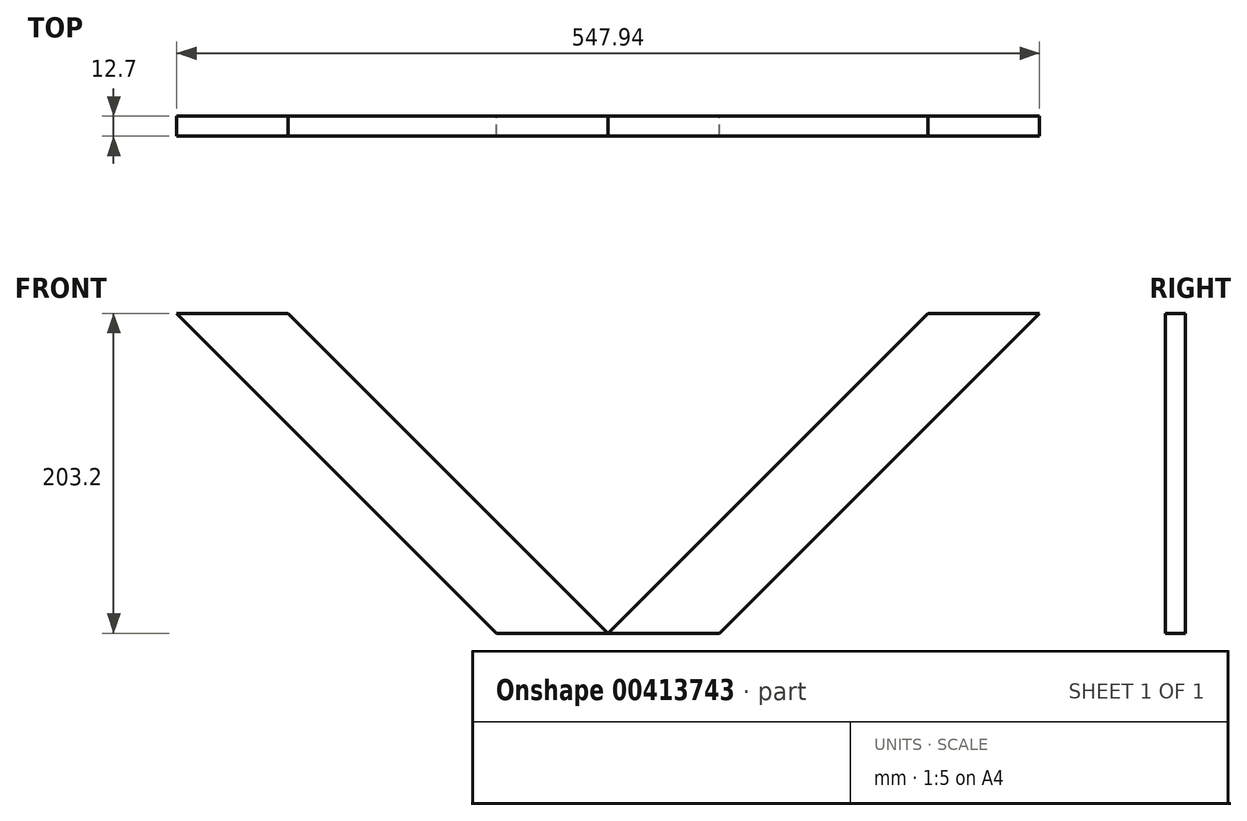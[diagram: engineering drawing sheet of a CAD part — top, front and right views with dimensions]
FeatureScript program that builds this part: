
annotation { "Feature Type Name" : "Feature", "Feature Type Description" : "" }
export const myFeature = defineFeature(function(context is Context, id is Id, definition is map)
    precondition{}
    {
        {
            var Q0;
            Q0=qCreatedBy(makeId("Front.planeOp"),FACE);
            var sketch = newSketch(context, id + "F0", { "sketchPlane" : qUnion([Q0])});
            skLineSegment(sketch, "E0", {"start": v(0, 0) * mm, "end": v(203.2, 203.2) * mm});
            skLineSegment(sketch, "E1", {"start": v(203.2, 203.2) * mm, "end": v(273.97, 203.2) * mm});
            skLineSegment(sketch, "E2", {"start": v(273.97, 203.2) * mm, "end": v(70.77, 0) * mm});
            skLineSegment(sketch, "E3", {"start": v(70.77, 0) * mm, "end": v(0, 0) * mm});
            skSolve(sketch);
        }
        {
            var Q0;
            Q0 = qSketchRegion(id + "F0", true);
            var sketch = newSketch(context, id + "F1", { "sketchPlane" : qUnion([Q0])});
            skSolve(sketch);
        }
        {
            var Q0;
            Q0=makeQuery(id+"F1.imprint","IMPRINT",FACE,{"disambiguationData":[TD([[makeQuery(id+"F1.imprint","IMPRINT",EDGE,{"derivedFrom":makeQuery(id+"F0.imprint","IMPRINT",EDGE,{"derivedFrom":sQuery(id+"F0.wireOp",EDGE,"E0")})}),-1.0]])]});
            extrude(context, id + "F2", {"entities" : qUnion([Q0]), "depth" : 12.7 * mm});
        }
        {
            var Q0;
            Q0=makeQuery(id+"F2.opExtrude","SWEPT_BODY",BODY,{"disambiguationData":[OSD([sQuery(id+"F0.wireOp",EDGE,"E0"),sQuery(id+"F0.wireOp",EDGE,"E1"),sQuery(id+"F0.wireOp",EDGE,"E2"),sQuery(id+"F0.wireOp",EDGE,"E3")])]});
            var Q1;
            Q1=qCreatedBy(makeId("Right.planeOp"),FACE);
            mirror(context, id + "F3", {"entities" : qUnion([Q0]), "mirrorPlane" : qUnion([Q1])});
        }
    });
